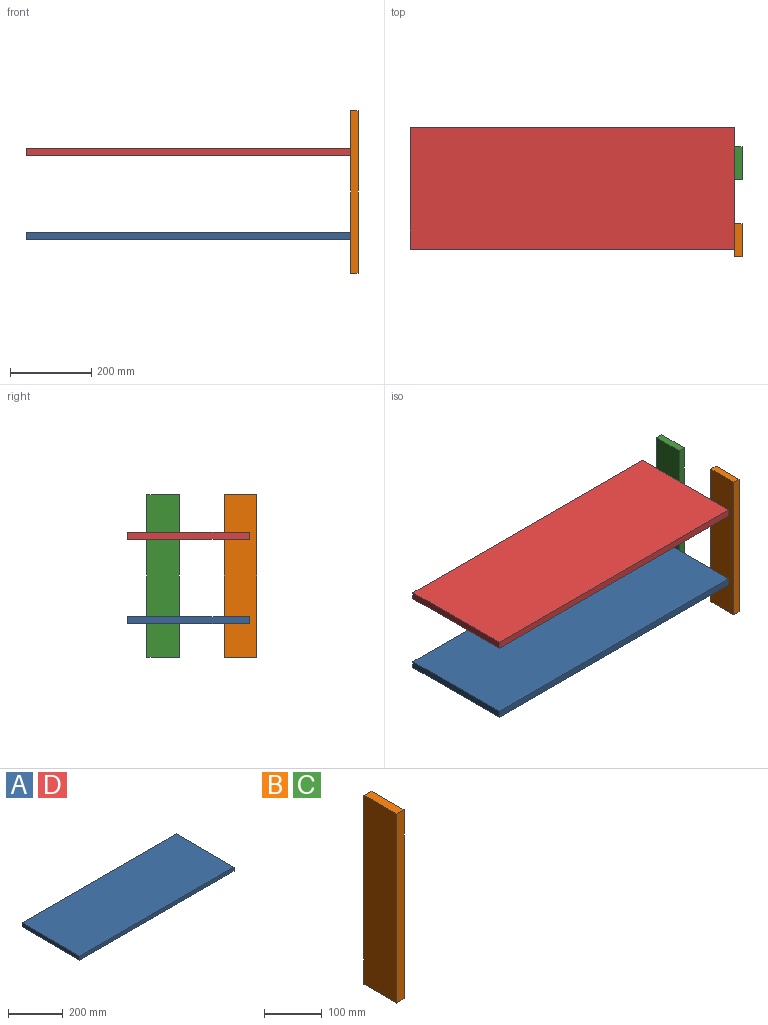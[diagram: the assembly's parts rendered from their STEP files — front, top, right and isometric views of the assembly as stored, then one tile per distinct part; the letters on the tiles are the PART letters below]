
ASSEMBLY  parts=4 mates=5
PART A: 6 faces, bbox 800x300x18 mm
  f0: plane 800x300mm, normal (0,0,-1), area 240000mm2, adj f1,f3,f4,f5
  f1: plane 800x18mm, normal (0,1,0), area 14400mm2, adj f0,f2,f4,f5
  f2: plane 800x300mm, normal (0,0,1), area 240000mm2, adj f1,f3,f4,f5
  f3: plane 800x18mm, normal (0,-1,0), area 14400mm2, adj f0,f2,f4,f5
  f4: plane 300x18mm, normal (1,0,0), area 5400mm2, adj f0,f1,f2,f3
  f5: plane 300x18mm, normal (-1,0,0), area 5400mm2, adj f0,f1,f2,f3
PART B: 6 faces, bbox 18x80x400 mm
  f0: plane 80x18mm, normal (0,0,1), area 1440mm2, adj f1,f3,f4,f5
  f1: plane 400x18mm, normal (0,-1,0), area 7200mm2, adj f0,f2,f4,f5
  f2: plane 80x18mm, normal (0,0,-1), area 1440mm2, adj f1,f3,f4,f5
  f3: plane 400x18mm, normal (0,1,0), area 7200mm2, adj f0,f2,f4,f5
  f4: plane 400x80mm, normal (1,0,0), area 32000mm2, adj f0,f1,f2,f3
  f5: plane 400x80mm, normal (-1,0,0), area 32000mm2, adj f0,f1,f2,f3
PART C: same geometry as B
PART D: same geometry as A
PLACE A t=(-136.58,90.75,-380.4)mm
PLACE B t=(663.42,-227.25,-62.4)mm
PLACE C t=(663.42,-37.25,-62.4)mm
PLACE D t=(-136.58,90.75,-172.4)mm
MATE planar A.f1 <-> D.f1  axis (0,1,0) through (263.42,90.75,-371.4)mm
MATE planar C.f5 <-> A.f4  axis (-1,0,0) through (663.42,2.75,-262.4)mm
MATE planar B.f5 <-> D.f4  axis (-1,0,0) through (663.42,-187.25,-262.4)mm
MATE planar C.f5 <-> D.f4  axis (-1,0,0) through (663.42,2.75,-262.4)mm
MATE planar B.f5 <-> A.f4  axis (-1,0,0) through (663.42,-187.25,-262.4)mm
